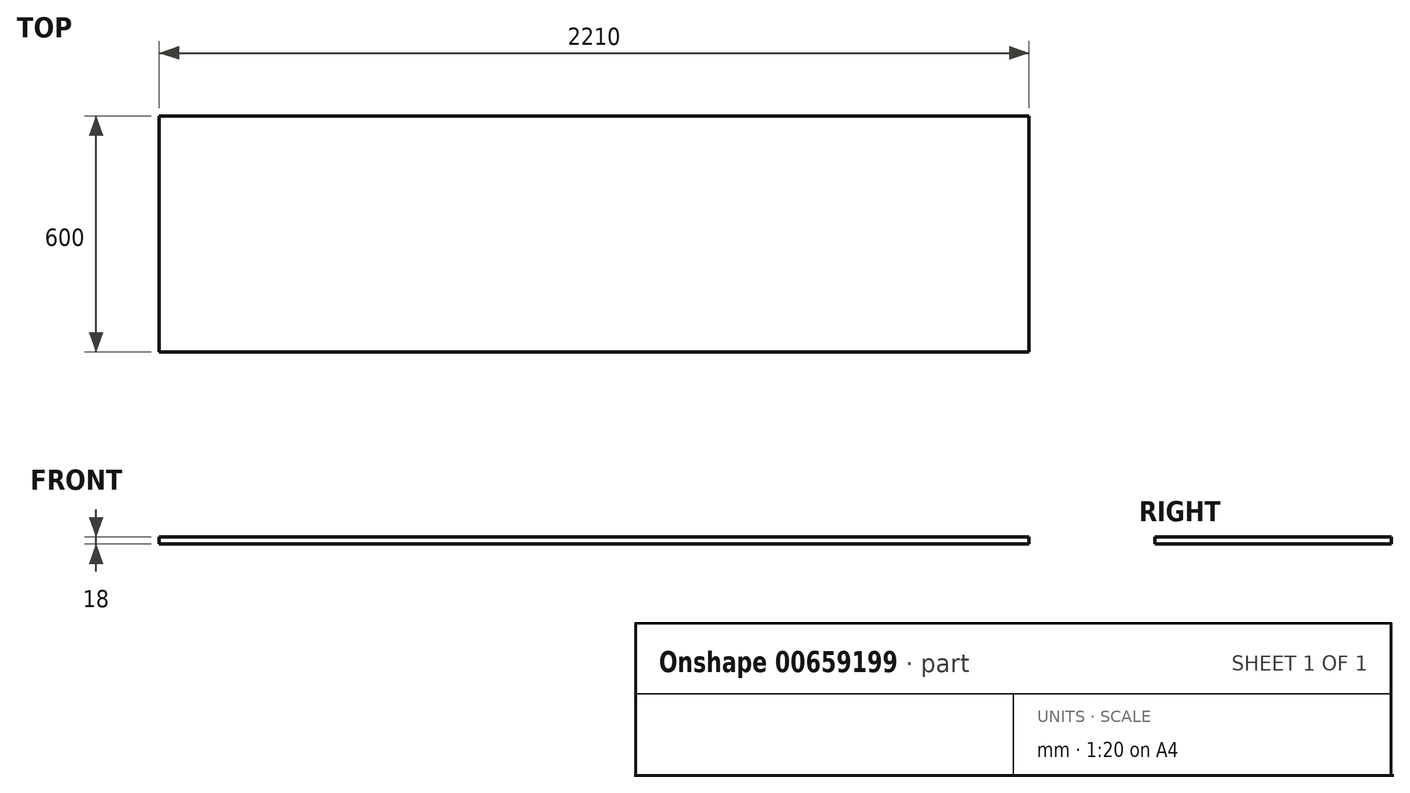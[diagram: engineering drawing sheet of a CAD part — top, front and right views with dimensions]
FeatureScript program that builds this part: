
annotation { "Feature Type Name" : "Feature", "Feature Type Description" : "" }
export const myFeature = defineFeature(function(context is Context, id is Id, definition is map)
    precondition{}
    {
        {
            var Q0;
            Q0=qCreatedBy(makeId("Top.planeOp"),FACE);
            var sketch = newSketch(context, id + "F0", { "sketchPlane" : qUnion([Q0])});
            skLineSegment(sketch, "E0.bottom", {"start": v(-261.85, 301.9) * mm, "end": v(1948.15, 301.9) * mm});
            skLineSegment(sketch, "E0.top", {"start": v(-261.85, -298.1) * mm, "end": v(1948.15, -298.1) * mm});
            skLineSegment(sketch, "E0.left", {"start": v(-261.85, 301.9) * mm, "end": v(-261.85, -298.1) * mm});
            skLineSegment(sketch, "E0.right", {"start": v(1948.15, 301.9) * mm, "end": v(1948.15, -298.1) * mm});
            skSolve(sketch);
        }
        {
            var Q0;
            Q0=qSketchRegion(id+"F0",true);
            extrude(context, id + "F1", {"entities" : qUnion([Q0]), "endBound" : BoundingType.SYMMETRIC, "depth" : 18 * mm, "offsetDistance" : 25 * mm});
        }
    });
